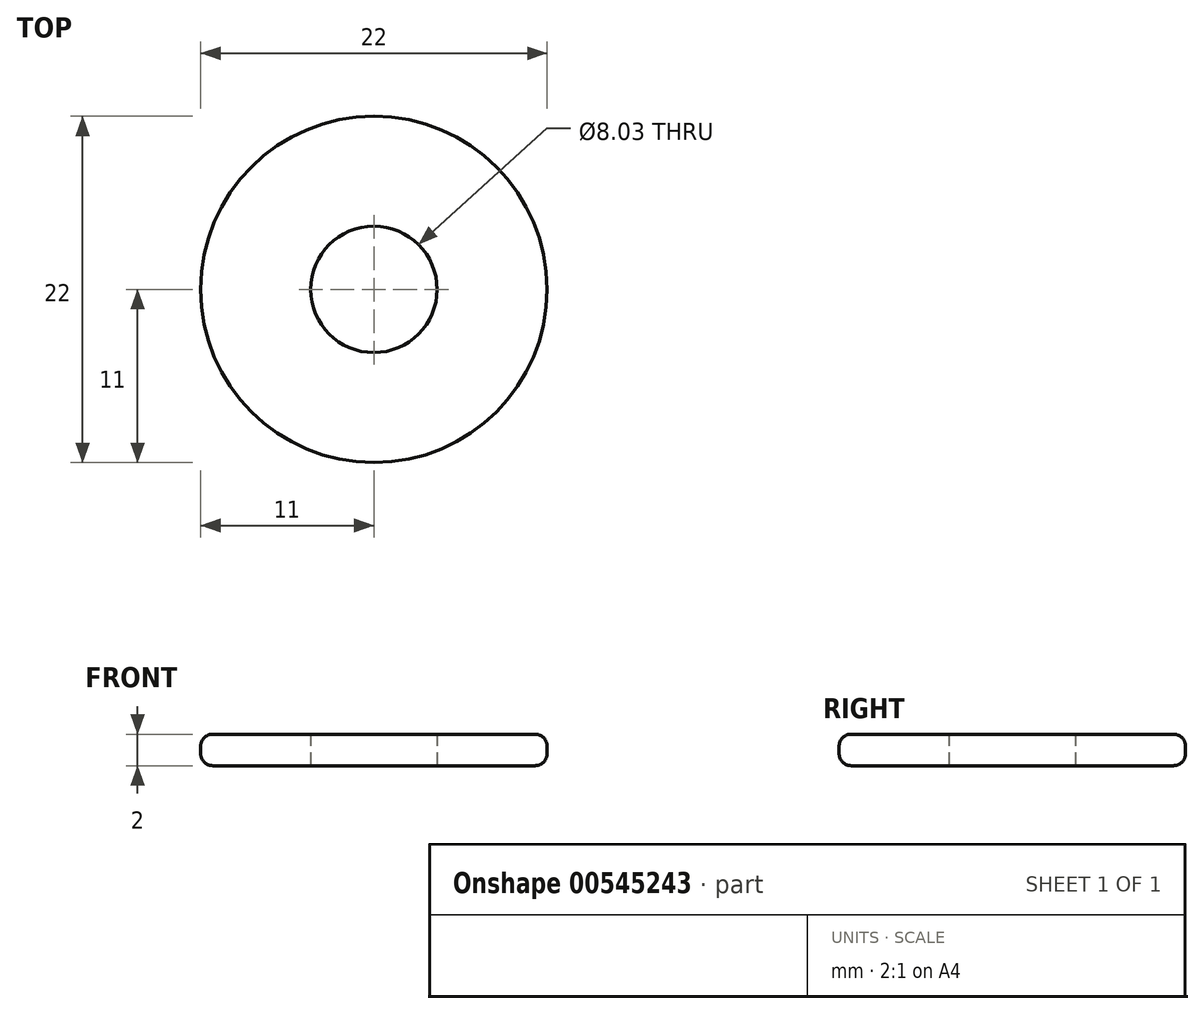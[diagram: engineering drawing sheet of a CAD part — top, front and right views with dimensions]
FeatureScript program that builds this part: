
annotation { "Feature Type Name" : "Feature", "Feature Type Description" : "" }
export const myFeature = defineFeature(function(context is Context, id is Id, definition is map)
    precondition{}
    {
        {
            var Q0;
            Q0=qCreatedBy(makeId("Top.planeOp"),FACE);
            var sketch = newSketch(context, id + "F0", { "sketchPlane" : qUnion([Q0])});
            skCircle(sketch, "E0", {"center": v(0, 0) * mm, "radius": 11 * mm});
            skSolve(sketch);
        }
        {
            var Q0;
            Q0 = qSketchRegion(id + "F0", true);
            extrude(context, id + "F1", {"entities" : qUnion([Q0]), "depth" : 2 * mm, "offsetDistance" : 25.4 * mm});
        }
        {
            var Q0;
            Q0=qCreatedBy(makeId("Top.planeOp"),FACE);
            var sketch = newSketch(context, id + "F2", { "sketchPlane" : qUnion([Q0])});
            skCircle(sketch, "E1", {"center": v(0, 0) * mm, "radius": 4.01 * mm});
            skSolve(sketch);
        }
        {
            var Q0;
            Q0=makeQuery(id+"F2.imprint","IMPRINT",FACE,{"disambiguationData":[TD([[makeQuery(id+"F2.imprint","IMPRINT",EDGE,{"derivedFrom":sQuery(id+"F2.wireOp",EDGE,"E1")}),1.0]])]});
            extrude(context, id + "F3", {"entities" : qUnion([Q0]), "operationType" : NewBodyOperationType.REMOVE, "depth" : 2 * mm, "offsetDistance" : 25.4 * mm});
        }
        {
            var Q0;
            Q0=makeQuery(id+"F1.opExtrude","CAP_EDGE",EDGE,{"disambiguationData":[OSD([sQuery(id+"F0.wireOp",EDGE,"E0")])],"isStart":false});
            var Q1;
            Q1=makeQuery(id+"F1.opExtrude","CAP_EDGE",EDGE,{"disambiguationData":[OSD([sQuery(id+"F0.wireOp",EDGE,"E0")])],"isStart":true});
            fillet(context, id + "F4", {"entities" : qUnion([Q0, Q1]), "radius" : 0.76 * mm, "tangentPropagation" : true, "allowEdgeOverflow" : false});
        }
    });
